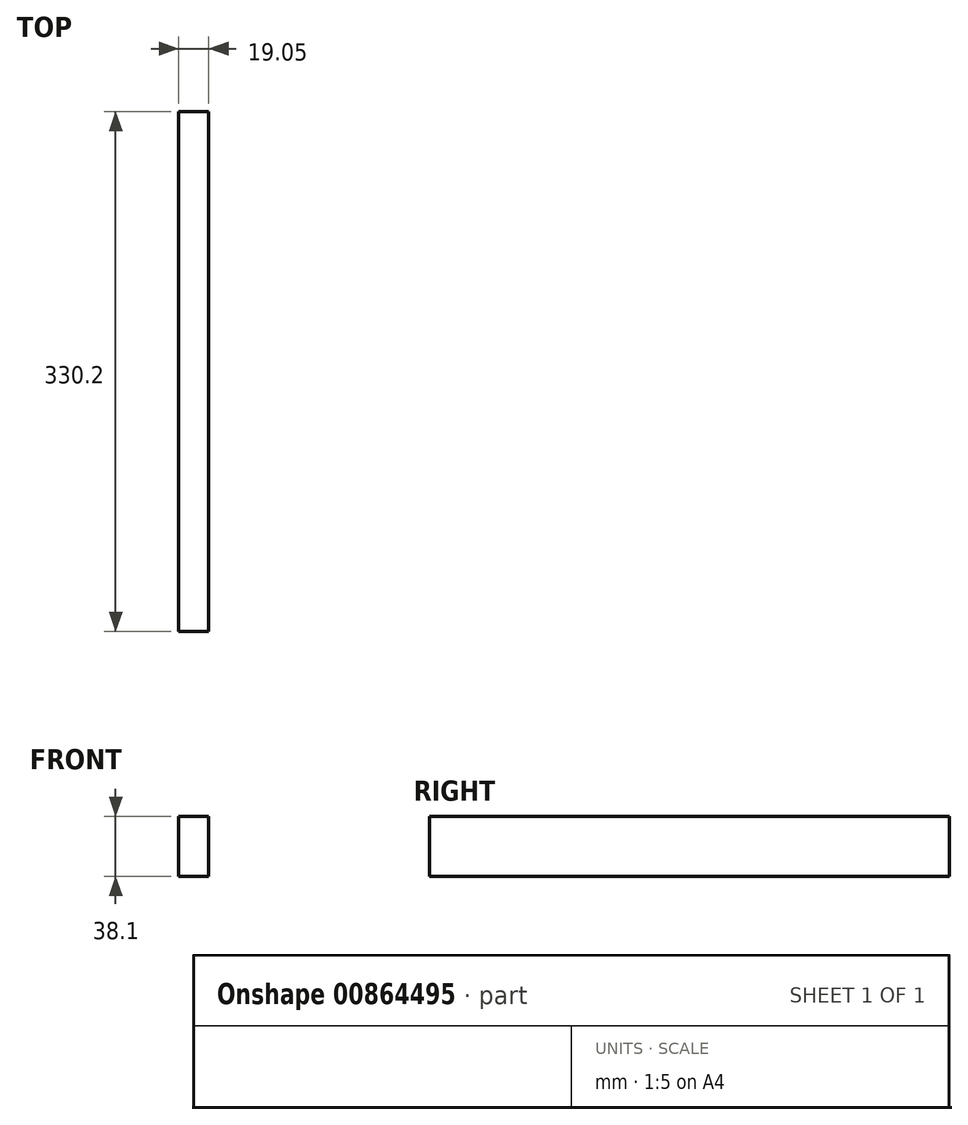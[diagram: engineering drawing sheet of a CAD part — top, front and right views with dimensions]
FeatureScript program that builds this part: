
annotation { "Feature Type Name" : "Feature", "Feature Type Description" : "" }
export const myFeature = defineFeature(function(context is Context, id is Id, definition is map)
    precondition{}
    {
        {
            var Q0;
            Q0=qCreatedBy(makeId("Right.planeOp"),FACE);
            var sketch = newSketch(context, id + "F0", { "sketchPlane" : qUnion([Q0])});
            skLineSegment(sketch, "E0.bottom", {"start": v(165.1, 19.05) * mm, "end": v(-165.1, 19.05) * mm});
            skLineSegment(sketch, "E0.top", {"start": v(165.1, -19.05) * mm, "end": v(-165.1, -19.05) * mm});
            skLineSegment(sketch, "E0.left", {"start": v(165.1, 19.05) * mm, "end": v(165.1, -19.05) * mm});
            skLineSegment(sketch, "E0.right", {"start": v(-165.1, 19.05) * mm, "end": v(-165.1, -19.05) * mm});
            skPoint(sketch, "E0.middle", {"position": v(0, 0) * mm});
            skSolve(sketch);
        }
        {
            var Q0;
            Q0=makeQuery(id+"F0.imprint","IMPRINT",FACE,{"disambiguationData":[TD([[makeQuery(id+"F0.imprint","IMPRINT",EDGE,{"derivedFrom":sQuery(id+"F0.wireOp",EDGE,"E0.bottom")}),1.0]])]});
            extrude(context, id + "F1", {"entities" : qUnion([Q0]), "depth" : 19.05 * mm, "offsetDistance" : 25.4 * mm});
        }
    });
